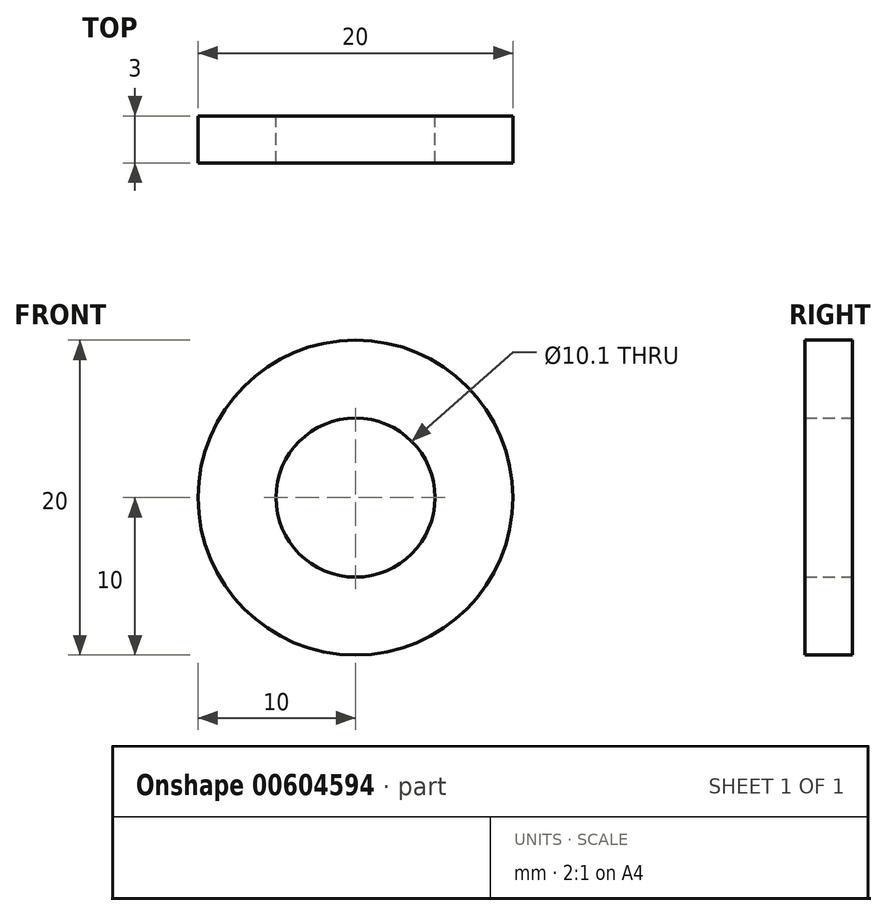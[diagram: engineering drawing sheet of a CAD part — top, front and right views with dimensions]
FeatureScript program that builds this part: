
annotation { "Feature Type Name" : "Feature", "Feature Type Description" : "" }
export const myFeature = defineFeature(function(context is Context, id is Id, definition is map)
    precondition{}
    {
        {
            var Q0;
            Q0=qCreatedBy(makeId("Front.planeOp"),FACE);
            var sketch = newSketch(context, id + "F0", { "sketchPlane" : qUnion([Q0])});
            skCircle(sketch, "E0", {"center": v(0, 0) * mm, "radius": 5.05 * mm});
            skCircle(sketch, "E1", {"center": v(0, 0) * mm, "radius": 10 * mm});
            skSolve(sketch);
        }
        {
            var Q0;
            Q0=makeQuery(id+"F0.imprint","IMPRINT",FACE,{"disambiguationData":[TD([[makeQuery(id+"F0.imprint","IMPRINT",EDGE,{"derivedFrom":sQuery(id+"F0.wireOp",EDGE,"E0")}),-1.0]])]});
            extrude(context, id + "F1", {"entities" : qUnion([Q0]), "depth" : 3 * mm, "offsetDistance" : 25 * mm});
        }
    });
